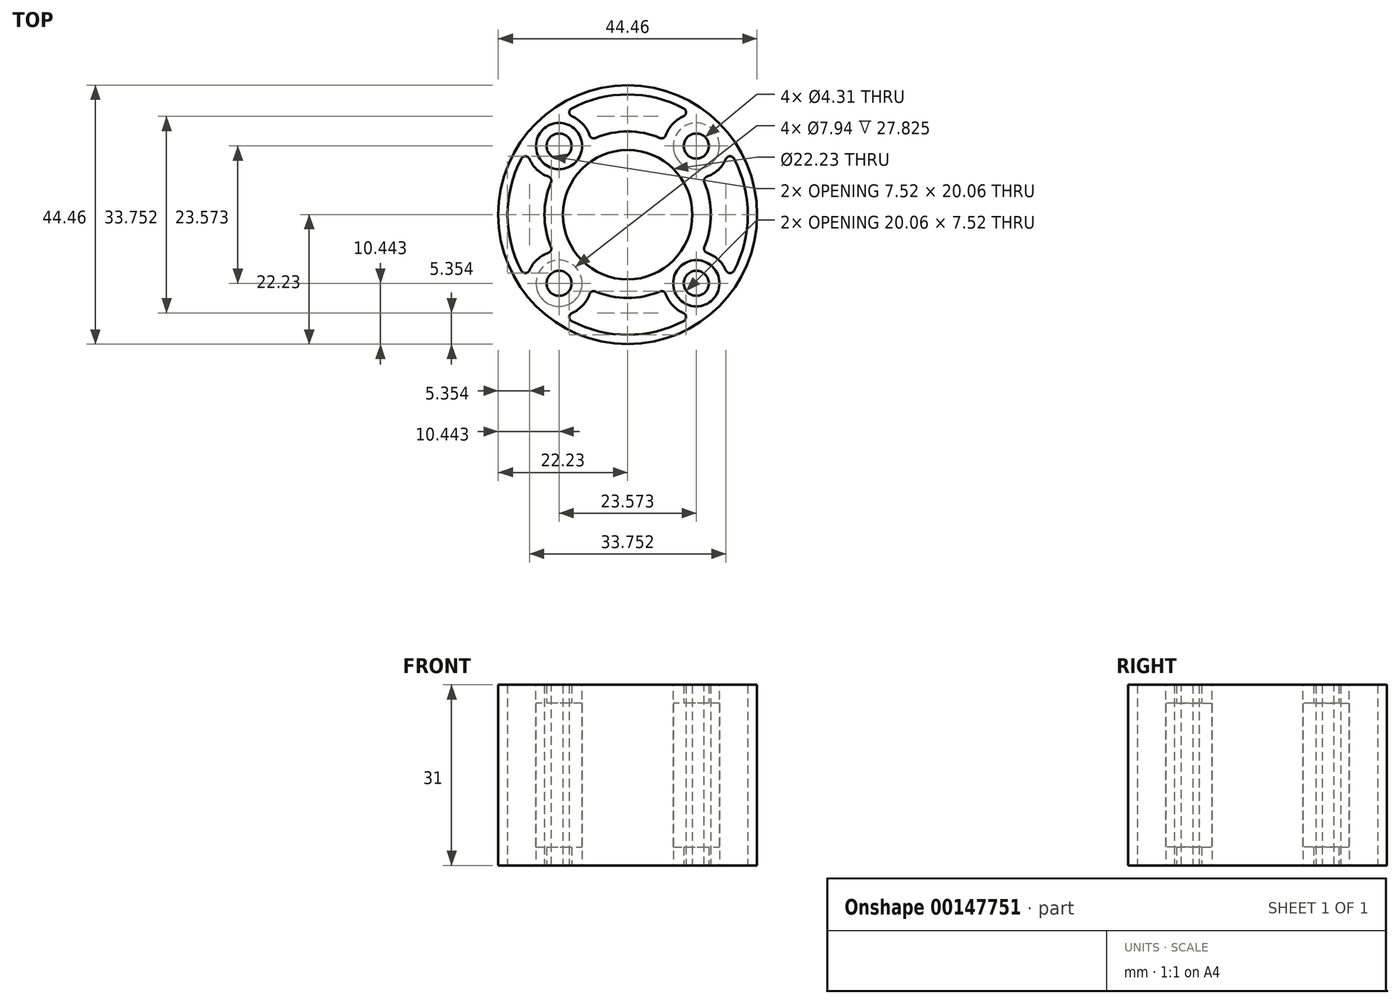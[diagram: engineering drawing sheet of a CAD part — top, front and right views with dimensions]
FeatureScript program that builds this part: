
annotation { "Feature Type Name" : "Feature", "Feature Type Description" : "" }
export const myFeature = defineFeature(function(context is Context, id is Id, definition is map)
    precondition{}
    {
        {
            var Q0;
            Q0=qCreatedBy(makeId("Top.planeOp"),FACE);
            var sketch = newSketch(context, id + "F0", { "sketchPlane" : qUnion([Q0])});
            skCircle(sketch, "E0", {"center": v(0, 0) * mm, "radius": 11.11 * mm});
            skLineSegment(sketch, "E1.bottom", {"start": v(11.79, 11.79) * mm, "end": v(-11.79, 11.79) * mm, "construction": true});
            skLineSegment(sketch, "E1.top", {"start": v(11.79, -11.79) * mm, "end": v(-11.79, -11.79) * mm, "construction": true});
            skLineSegment(sketch, "E1.left", {"start": v(11.79, 11.79) * mm, "end": v(11.79, -11.79) * mm, "construction": true});
            skLineSegment(sketch, "E1.right", {"start": v(-11.79, 11.79) * mm, "end": v(-11.79, -11.79) * mm, "construction": true});
            skCircle(sketch, "E2", {"center": v(-11.79, 11.79) * mm, "radius": 5.56 * mm, "construction": true});
            skCircle(sketch, "E3", {"center": v(-11.79, 11.79) * mm, "radius": 2.15 * mm});
            skCircle(sketch, "E4", {"center": v(-11.79, -11.79) * mm, "radius": 2.15 * mm});
            skCircle(sketch, "E5", {"center": v(11.79, -11.79) * mm, "radius": 2.15 * mm});
            skCircle(sketch, "E6", {"center": v(11.79, 11.79) * mm, "radius": 2.15 * mm});
            skCircle(sketch, "E7", {"center": v(0, 0) * mm, "radius": 22.22 * mm});
            skCircle(sketch, "E8", {"center": v(0, 0) * mm, "radius": 9.53 * mm, "construction": true});
            skSolve(sketch);
        }
        {
            var Q0;
            Q0=qSketchRegion(id+"F0",true);
            extrude(context, id + "F1", {"entities" : qUnion([Q0]), "depth" : 31 * mm});
        }
        {
            var Q0;
            Q0=makeQuery(id+"F1.opExtrude","CAP_FACE",FACE,{"disambiguationData":[OSD([sQuery(id+"F0.wireOp",EDGE,"E0"),sQuery(id+"F0.wireOp",EDGE,"E3"),sQuery(id+"F0.wireOp",EDGE,"E4"),sQuery(id+"F0.wireOp",EDGE,"E5"),sQuery(id+"F0.wireOp",EDGE,"E6"),sQuery(id+"F0.wireOp",EDGE,"E7")])],"isStart":true});
            var sketch = newSketch(context, id + "F2", { "sketchPlane" : qUnion([Q0])});
            skArc(sketch, "E9", {"start": v(6.33, -12.81) * mm, "mid": v(8.03, -15.88) * mm, "end": v(11.23, -17.31) * mm});
            skArc(sketch, "E10", {"start": v(-11.23, -17.31) * mm, "mid": v(0, -20.64) * mm, "end": v(11.23, -17.31) * mm});
            skArc(sketch, "E11", {"start": v(-6.33, -12.81) * mm, "mid": v(0, -14.29) * mm, "end": v(6.33, -12.81) * mm});
            skArc(sketch, "E12", {"start": v(-11.23, -17.31) * mm, "mid": v(-8.03, -15.88) * mm, "end": v(-6.33, -12.81) * mm});
            skSolve(sketch);
        }
        {
            var Q0;
            Q0=qSketchRegion(id+"F2",true);
            var Q1;
            Q1=makeQuery(id+"F1.opExtrude","CAP_FACE",FACE,{"disambiguationData":[OSD([sQuery(id+"F0.wireOp",EDGE,"E0"),sQuery(id+"F0.wireOp",EDGE,"E3"),sQuery(id+"F0.wireOp",EDGE,"E4"),sQuery(id+"F0.wireOp",EDGE,"E5"),sQuery(id+"F0.wireOp",EDGE,"E6"),sQuery(id+"F0.wireOp",EDGE,"E7")])],"isStart":false});
            extrude(context, id + "F3", {"entities" : qUnion([Q0]), "operationType" : NewBodyOperationType.REMOVE, "endBound" : BoundingType.UP_TO_SURFACE, "oppositeDirection" : true, "endBoundEntityFace" : qUnion([Q1]), "depth" : 25.4 * mm});
        }
        {
            var Q0;
            Q0=makeQuery(id+"F3.boolean.opBoolean","COPY",EDGE,{"derivedFrom":makeQuery(id+"F3.opExtrude","SWEPT_EDGE",EDGE,{"disambiguationData":[OSD([sQuery(id+"F2.wireOp",EDGE,"E11"),sQuery(id+"F2.wireOp",EDGE,"E12")])]})});
            var Q1;
            Q1=makeQuery(id+"F5.opPattern","COPY",EDGE,{"derivedFrom":makeQuery(id+"F3.boolean.opBoolean","COPY",EDGE,{"derivedFrom":makeQuery(id+"F3.opExtrude","SWEPT_EDGE",EDGE,{"disambiguationData":[OSD([sQuery(id+"F2.wireOp",EDGE,"E9"),sQuery(id+"F2.wireOp",EDGE,"E11")])]})}),"instanceName":"3"});
            var Q2;
            Q2=makeQuery(id+"F5.opPattern","COPY",EDGE,{"derivedFrom":makeQuery(id+"F3.boolean.opBoolean","COPY",EDGE,{"derivedFrom":makeQuery(id+"F3.opExtrude","SWEPT_EDGE",EDGE,{"disambiguationData":[OSD([sQuery(id+"F2.wireOp",EDGE,"E11"),sQuery(id+"F2.wireOp",EDGE,"E12")])]})}),"instanceName":"3"});
            var Q3;
            Q3=makeQuery(id+"F5.opPattern","COPY",EDGE,{"derivedFrom":makeQuery(id+"F3.boolean.opBoolean","COPY",EDGE,{"derivedFrom":makeQuery(id+"F3.opExtrude","SWEPT_EDGE",EDGE,{"disambiguationData":[OSD([sQuery(id+"F2.wireOp",EDGE,"E9"),sQuery(id+"F2.wireOp",EDGE,"E11")])]})}),"instanceName":"2"});
            var Q4;
            Q4=makeQuery(id+"F5.opPattern","COPY",EDGE,{"derivedFrom":makeQuery(id+"F3.boolean.opBoolean","COPY",EDGE,{"derivedFrom":makeQuery(id+"F3.opExtrude","SWEPT_EDGE",EDGE,{"disambiguationData":[OSD([sQuery(id+"F2.wireOp",EDGE,"E11"),sQuery(id+"F2.wireOp",EDGE,"E12")])]})}),"instanceName":"2"});
            var Q5;
            Q5=makeQuery(id+"F5.opPattern","COPY",EDGE,{"derivedFrom":makeQuery(id+"F3.boolean.opBoolean","COPY",EDGE,{"derivedFrom":makeQuery(id+"F3.opExtrude","SWEPT_EDGE",EDGE,{"disambiguationData":[OSD([sQuery(id+"F2.wireOp",EDGE,"E9"),sQuery(id+"F2.wireOp",EDGE,"E11")])]})}),"instanceName":"1"});
            var Q6;
            Q6=makeQuery(id+"F5.opPattern","COPY",EDGE,{"derivedFrom":makeQuery(id+"F3.boolean.opBoolean","COPY",EDGE,{"derivedFrom":makeQuery(id+"F3.opExtrude","SWEPT_EDGE",EDGE,{"disambiguationData":[OSD([sQuery(id+"F2.wireOp",EDGE,"E11"),sQuery(id+"F2.wireOp",EDGE,"E12")])]})}),"instanceName":"1"});
            var Q7;
            Q7=makeQuery(id+"F3.boolean.opBoolean","COPY",EDGE,{"derivedFrom":makeQuery(id+"F3.opExtrude","SWEPT_EDGE",EDGE,{"disambiguationData":[OSD([sQuery(id+"F2.wireOp",EDGE,"E9"),sQuery(id+"F2.wireOp",EDGE,"E11")])]})});
            var Q8;
            Q8=makeQuery(id+"F3.boolean.opBoolean","COPY",EDGE,{"derivedFrom":makeQuery(id+"F3.opExtrude","SWEPT_EDGE",EDGE,{"disambiguationData":[OSD([sQuery(id+"F2.wireOp",EDGE,"E9"),sQuery(id+"F2.wireOp",EDGE,"E10")])]})});
            var Q9;
            Q9=makeQuery(id+"F3.boolean.opBoolean","COPY",EDGE,{"derivedFrom":makeQuery(id+"F3.opExtrude","SWEPT_EDGE",EDGE,{"disambiguationData":[OSD([sQuery(id+"F2.wireOp",EDGE,"E10"),sQuery(id+"F2.wireOp",EDGE,"E12")])]})});
            fillet(context, id + "F4", {"entities" : qUnion([Q0, Q1, Q2, Q3, Q4, Q5, Q6, Q7, Q8, Q9]), "radius" : 0.76 * mm, "tangentPropagation" : true, "allowEdgeOverflow" : false});
        }
        {
            var Q0;
            Q0=makeQuery(id+"F3.boolean.opBoolean","COPY",FACE,{"derivedFrom":makeQuery(id+"F3.opExtrude","SWEPT_FACE",FACE,{"disambiguationData":[OSD([sQuery(id+"F2.wireOp",EDGE,"E10")])]})});
            var Q1;
            Q1=makeQuery(id+"F3.boolean.opBoolean","COPY",FACE,{"derivedFrom":makeQuery(id+"F3.opExtrude","SWEPT_FACE",FACE,{"disambiguationData":[OSD([sQuery(id+"F2.wireOp",EDGE,"E12")])]})});
            var Q2;
            Q2=makeQuery(id+"F3.boolean.opBoolean","COPY",FACE,{"derivedFrom":makeQuery(id+"F3.opExtrude","SWEPT_FACE",FACE,{"disambiguationData":[OSD([sQuery(id+"F2.wireOp",EDGE,"E11")])]})});
            var Q3;
            Q3=makeQuery(id+"F3.boolean.opBoolean","COPY",FACE,{"derivedFrom":makeQuery(id+"F3.opExtrude","SWEPT_FACE",FACE,{"disambiguationData":[OSD([sQuery(id+"F2.wireOp",EDGE,"E9")])]})});
            var Q4;
            Q4=makeQuery(id+"F4.opFillet","BLEND_FACE",FACE,{"disambiguationData":[OSD([sQuery(id+"F2.wireOp",EDGE,"E9"),sQuery(id+"F2.wireOp",EDGE,"E10")])]});
            var Q5;
            Q5=makeQuery(id+"F4.opFillet","BLEND_FACE",FACE,{"disambiguationData":[OSD([sQuery(id+"F2.wireOp",EDGE,"E9"),sQuery(id+"F2.wireOp",EDGE,"E11")])]});
            var Q6;
            Q6=makeQuery(id+"F4.opFillet","BLEND_FACE",FACE,{"disambiguationData":[OSD([sQuery(id+"F2.wireOp",EDGE,"E10"),sQuery(id+"F2.wireOp",EDGE,"E12")])]});
            var Q7;
            Q7=makeQuery(id+"F4.opFillet","BLEND_FACE",FACE,{"disambiguationData":[OSD([sQuery(id+"F2.wireOp",EDGE,"E11"),sQuery(id+"F2.wireOp",EDGE,"E12")])]});
            var Q8;
            Q8=makeQuery(id+"F1.opExtrude","SWEPT_FACE",FACE,{"disambiguationData":[OSD([sQuery(id+"F0.wireOp",EDGE,"E7")])]});
            circularPattern(context, id + "F5", {"patternType" : PatternType.FACE, "faces" : qUnion([Q0, Q1, Q2, Q3, Q4, Q5, Q6, Q7]), "axis" : qUnion([Q8]), "angle" : 90 * degree, "instanceCount" : 4});
        }
        {
            var Q0;
            Q0=makeQuery(id+"F1.opExtrude","CAP_FACE",FACE,{"disambiguationData":[OSD([sQuery(id+"F0.wireOp",EDGE,"E3"),sQuery(id+"F0.wireOp",EDGE,"E4"),sQuery(id+"F0.wireOp",EDGE,"E5"),sQuery(id+"F0.wireOp",EDGE,"E6"),sQuery(id+"F0.wireOp",EDGE,"E7"),sQuery(id+"F0.wireOp",EDGE,"E8")])],"isStart":true});
            var sketch = newSketch(context, id + "F6", { "sketchPlane" : qUnion([Q0])});
            skCircle(sketch, "E13", {"center": v(11.79, -11.79) * mm, "radius": 3.97 * mm});
            skCircle(sketch, "E14", {"center": v(-11.79, 11.79) * mm, "radius": 3.97 * mm});
            skSolve(sketch);
        }
        {
            var Q0;
            Q0=makeQuery(id+"F1.opExtrude","CAP_FACE",FACE,{"disambiguationData":[OSD([sQuery(id+"F0.wireOp",EDGE,"E3"),sQuery(id+"F0.wireOp",EDGE,"E4"),sQuery(id+"F0.wireOp",EDGE,"E5"),sQuery(id+"F0.wireOp",EDGE,"E6"),sQuery(id+"F0.wireOp",EDGE,"E7"),sQuery(id+"F0.wireOp",EDGE,"E8")])],"isStart":false});
            var sketch = newSketch(context, id + "F7", { "sketchPlane" : qUnion([Q0])});
            skCircle(sketch, "E15", {"center": v(-11.79, 11.79) * mm, "radius": 3.97 * mm});
            skCircle(sketch, "E16", {"center": v(11.79, -11.79) * mm, "radius": 3.97 * mm});
            skSolve(sketch);
        }
        {
            var Q0;
            Q0=makeQuery(id+"F7.imprint","IMPRINT",FACE,{"disambiguationData":[TD([[makeQuery(id+"F7.imprint","IMPRINT",EDGE,{"derivedFrom":sQuery(id+"F7.wireOp",EDGE,"E15")}),-1.0]])]});
            cPlane(context, id + "F8", {"entities" : qUnion([Q0]), "cplaneType" : CPlaneType.OFFSET, "offset" : 3.17 * mm, "oppositeDirection" : true, "width" : 152.4 * mm, "height" : 152.4 * mm});
        }
        {
            var Q0;
            Q0=makeQuery(id+"F6.imprint","IMPRINT",FACE,{"disambiguationData":[TD([[makeQuery(id+"F6.imprint","IMPRINT",EDGE,{"derivedFrom":sQuery(id+"F6.wireOp",EDGE,"E13")}),-1.0]])]});
            cPlane(context, id + "F9", {"entities" : qUnion([Q0]), "cplaneType" : CPlaneType.OFFSET, "offset" : 3.17 * mm, "oppositeDirection" : true, "width" : 152.4 * mm, "height" : 152.4 * mm});
        }
        {
            var Q0;
            Q0=makeQuery(id+"F7.imprint","IMPRINT",FACE,{"disambiguationData":[TD([[makeQuery(id+"F7.imprint","IMPRINT",EDGE,{"derivedFrom":sQuery(id+"F7.wireOp",EDGE,"E15")}),1.0]])]});
            var Q1;
            Q1=makeQuery(id+"F7.imprint","IMPRINT",FACE,{"disambiguationData":[TD([[makeQuery(id+"F7.imprint","IMPRINT",EDGE,{"derivedFrom":sQuery(id+"F7.wireOp",EDGE,"E16")}),1.0]])]});
            var Q2;
            Q2=sQuery(id+"F7.wireOp",EDGE,"E15");
            var Q3;
            Q3=sQuery(id+"F7.wireOp",EDGE,"E16");
            var Q4;
            Q4=qCreatedBy(id+"F9.planeOp",FACE);
            extrude(context, id + "F10", {"entities" : qUnion([Q0, Q1]), "operationType" : NewBodyOperationType.REMOVE, "surfaceEntities" : qUnion([Q2, Q3]), "endBound" : BoundingType.UP_TO_SURFACE, "oppositeDirection" : true, "endBoundEntityFace" : qUnion([Q4]), "depth" : 25.4 * mm});
        }
        {
            var Q0;
            Q0=makeQuery(id+"F6.imprint","IMPRINT",FACE,{"disambiguationData":[TD([[makeQuery(id+"F6.imprint","IMPRINT",EDGE,{"derivedFrom":sQuery(id+"F6.wireOp",EDGE,"E13")}),1.0]])]});
            var Q1;
            Q1=makeQuery(id+"F6.imprint","IMPRINT",FACE,{"disambiguationData":[TD([[makeQuery(id+"F6.imprint","IMPRINT",EDGE,{"derivedFrom":sQuery(id+"F6.wireOp",EDGE,"E14")}),1.0]])]});
            var Q2;
            Q2=qCreatedBy(id+"F8.planeOp",FACE);
            extrude(context, id + "F11", {"entities" : qUnion([Q0, Q1]), "operationType" : NewBodyOperationType.REMOVE, "endBound" : BoundingType.UP_TO_SURFACE, "oppositeDirection" : true, "endBoundEntityFace" : qUnion([Q2]), "depth" : 25.4 * mm});
        }
    });
